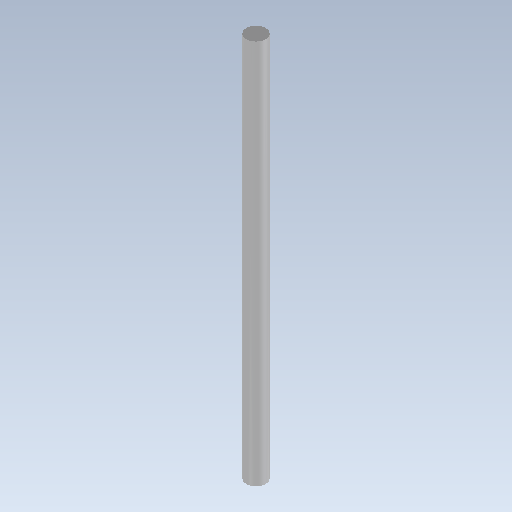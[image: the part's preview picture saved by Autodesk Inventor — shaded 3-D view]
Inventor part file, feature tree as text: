
AUTODESK INVENTOR PART (.ipt)
format: ipt  version: 2020 (Build 240168000, 168)  size: 76,288 bytes
history: native  units: mm
features: extrude x1, sketch x1
ambient origin geometry x8: Origin, YZ Plane, XZ Plane, XY Plane, X Axis, Y Axis, Z Axis, Center Point
bodies: Solid1 (feature_tree)
feature tree (2):
  extrude  "Extrusion1"  Depth=59.0mm TaperAngle=0.0deg
  sketch  "Sketch1"  dims[d0=3.0mm d1=59.0mm d2=0.0mm]
